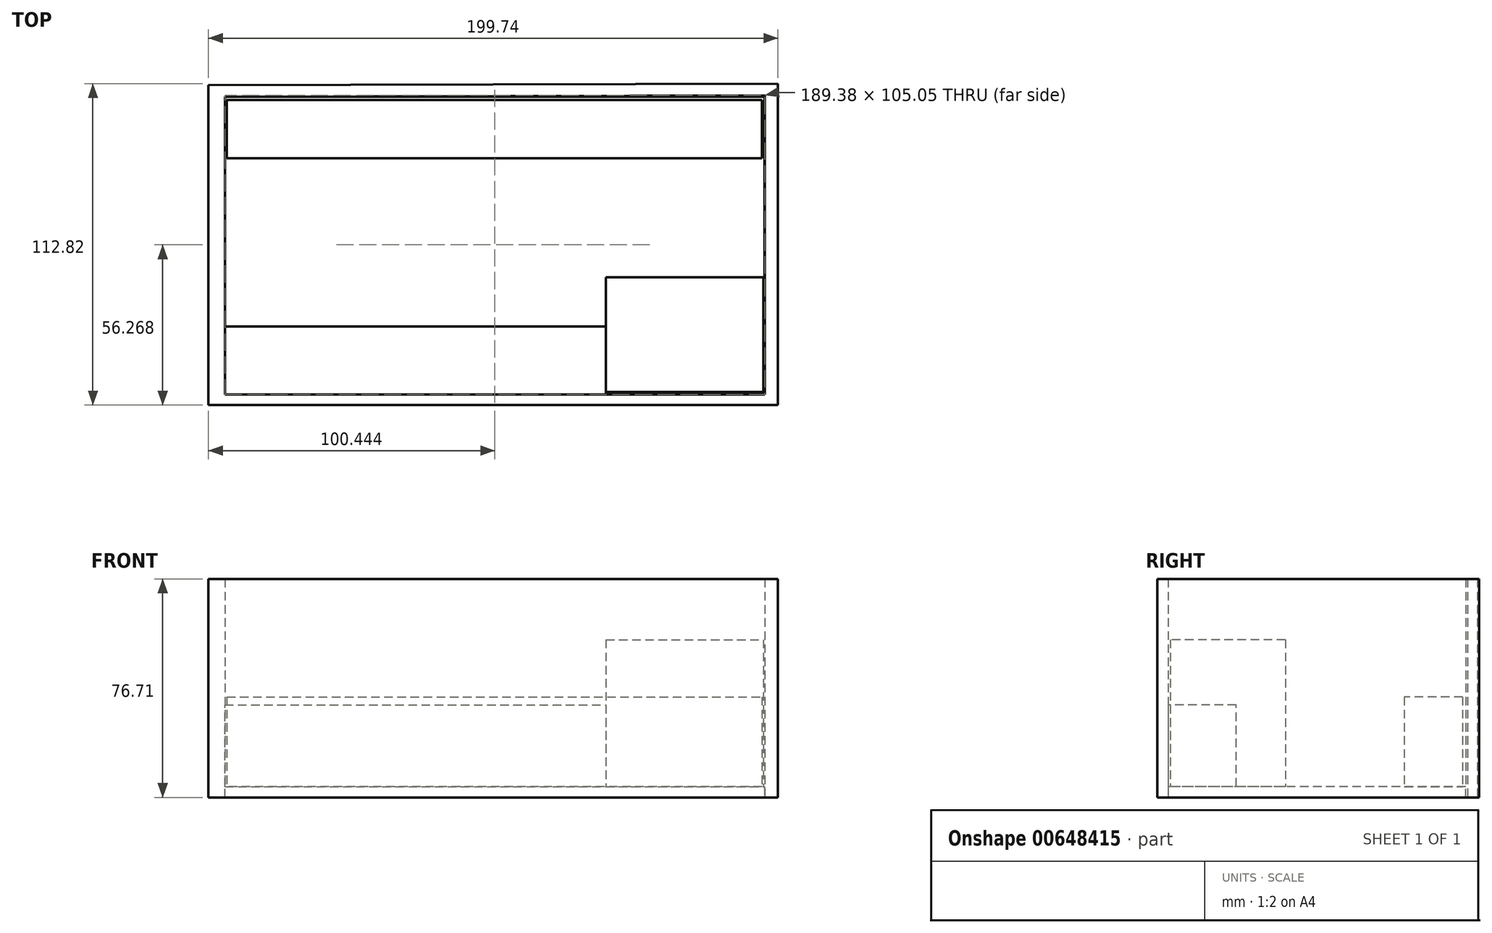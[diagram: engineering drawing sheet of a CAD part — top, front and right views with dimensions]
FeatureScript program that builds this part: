
annotation { "Feature Type Name" : "Feature", "Feature Type Description" : "" }
export const myFeature = defineFeature(function(context is Context, id is Id, definition is map)
    precondition{}
    {
        {
            var Q0;
            Q0=qCreatedBy(makeId("Top.planeOp"),FACE);
            var sketch = newSketch(context, id + "F0", { "sketchPlane" : qUnion([Q0])});
            skLineSegment(sketch, "E0", {"start": v(-100.3, 56.27) * mm, "end": v(-100.3, -55.98) * mm});
            skLineSegment(sketch, "E1", {"start": v(-100.3, -55.98) * mm, "end": v(99.44, -55.98) * mm});
            skLineSegment(sketch, "E2", {"start": v(99.44, -55.98) * mm, "end": v(99.44, 56.84) * mm});
            skLineSegment(sketch, "E3", {"start": v(99.44, 56.84) * mm, "end": v(-100.3, 56.27) * mm});
            skLineSegment(sketch, "E4", {"start": v(-94.54, 52.24) * mm, "end": v(-94.54, -52.24) * mm});
            skLineSegment(sketch, "E5", {"start": v(-94.54, -52.24) * mm, "end": v(94.83, -52.24) * mm});
            skLineSegment(sketch, "E6", {"start": v(94.83, -52.24) * mm, "end": v(94.83, 52.81) * mm});
            skLineSegment(sketch, "E7", {"start": v(94.83, 52.81) * mm, "end": v(-94.54, 52.24) * mm});
            skSolve(sketch);
        }
        {
            var Q0;
            Q0 = qSketchRegion(id + "F0", true);
            extrude(context, id + "F1", {"entities" : qUnion([Q0]), "depth" : 76.7 * mm, "offsetDistance" : 25.4 * mm});
        }
        {
            var Q0;
            Q0=qCreatedBy(makeId("Top.planeOp"),FACE);
            var sketch = newSketch(context, id + "F2", { "sketchPlane" : qUnion([Q0])});
            skLineSegment(sketch, "E8.bottom", {"start": v(-94.69, -28.35) * mm, "end": v(39.14, -28.35) * mm});
            skLineSegment(sketch, "E8.top", {"start": v(-94.69, -52.24) * mm, "end": v(39.14, -52.24) * mm});
            skLineSegment(sketch, "E8.left", {"start": v(-94.69, -28.35) * mm, "end": v(-94.69, -52.24) * mm});
            skLineSegment(sketch, "E8.right", {"start": v(39.14, -28.35) * mm, "end": v(39.14, -52.24) * mm});
            skSolve(sketch);
        }
        {
            var Q0;
            Q0 = qSketchRegion(id + "F2", true);
            extrude(context, id + "F3", {"entities" : qUnion([Q0]), "operationType" : NewBodyOperationType.ADD, "depth" : 32.5 * mm, "offsetDistance" : 25.4 * mm});
        }
        {
            var Q0;
            Q0=qCreatedBy(makeId("Top.planeOp"),FACE);
            var sketch = newSketch(context, id + "F4", { "sketchPlane" : qUnion([Q0])});
            skLineSegment(sketch, "E9.bottom", {"start": v(39.14, -11.08) * mm, "end": v(94.4, -11.08) * mm});
            skLineSegment(sketch, "E9.top", {"start": v(39.14, -51.37) * mm, "end": v(94.4, -51.37) * mm});
            skLineSegment(sketch, "E9.left", {"start": v(39.14, -11.08) * mm, "end": v(39.14, -51.37) * mm});
            skLineSegment(sketch, "E9.right", {"start": v(94.4, -11.08) * mm, "end": v(94.4, -51.37) * mm});
            skSolve(sketch);
        }
        {
            var Q0;
            Q0 = qSketchRegion(id + "F4", true);
            extrude(context, id + "F5", {"entities" : qUnion([Q0]), "operationType" : NewBodyOperationType.ADD, "depth" : 55.37 * mm, "offsetDistance" : 25.4 * mm});
        }
        {
            var Q0;
            Q0=qCreatedBy(makeId("Top.planeOp"),FACE);
            var sketch = newSketch(context, id + "F6", { "sketchPlane" : qUnion([Q0])});
            skLineSegment(sketch, "E10.bottom", {"start": v(-94.69, 52.24) * mm, "end": v(94.69, 52.24) * mm});
            skLineSegment(sketch, "E10.top", {"start": v(-94.69, -52.52) * mm, "end": v(94.69, -52.52) * mm});
            skLineSegment(sketch, "E10.left", {"start": v(-94.69, 52.24) * mm, "end": v(-94.69, -52.52) * mm});
            skLineSegment(sketch, "E10.right", {"start": v(94.69, 52.24) * mm, "end": v(94.69, -52.52) * mm});
            skSolve(sketch);
        }
        {
            var Q0;
            Q0 = qSketchRegion(id + "F6", true);
            extrude(context, id + "F7", {"entities" : qUnion([Q0]), "operationType" : NewBodyOperationType.ADD, "depth" : 3.8 * mm, "offsetDistance" : 25.4 * mm});
        }
        {
            var Q0;
            Q0=qCreatedBy(makeId("Top.planeOp"),FACE);
            var sketch = newSketch(context, id + "F8", { "sketchPlane" : qUnion([Q0])});
            skLineSegment(sketch, "E11.bottom", {"start": v(-93.82, 51.09) * mm, "end": v(93.82, 51.09) * mm});
            skLineSegment(sketch, "E11.top", {"start": v(-93.82, 30.65) * mm, "end": v(93.82, 30.65) * mm});
            skLineSegment(sketch, "E11.left", {"start": v(-93.82, 51.09) * mm, "end": v(-93.82, 30.65) * mm});
            skLineSegment(sketch, "E11.right", {"start": v(93.82, 51.09) * mm, "end": v(93.82, 30.65) * mm});
            skSolve(sketch);
        }
        {
            var Q0;
            Q0 = qSketchRegion(id + "F8", true);
            extrude(context, id + "F9", {"entities" : qUnion([Q0]), "operationType" : NewBodyOperationType.ADD, "depth" : 35.3 * mm, "offsetDistance" : 25.4 * mm});
        }
    });
